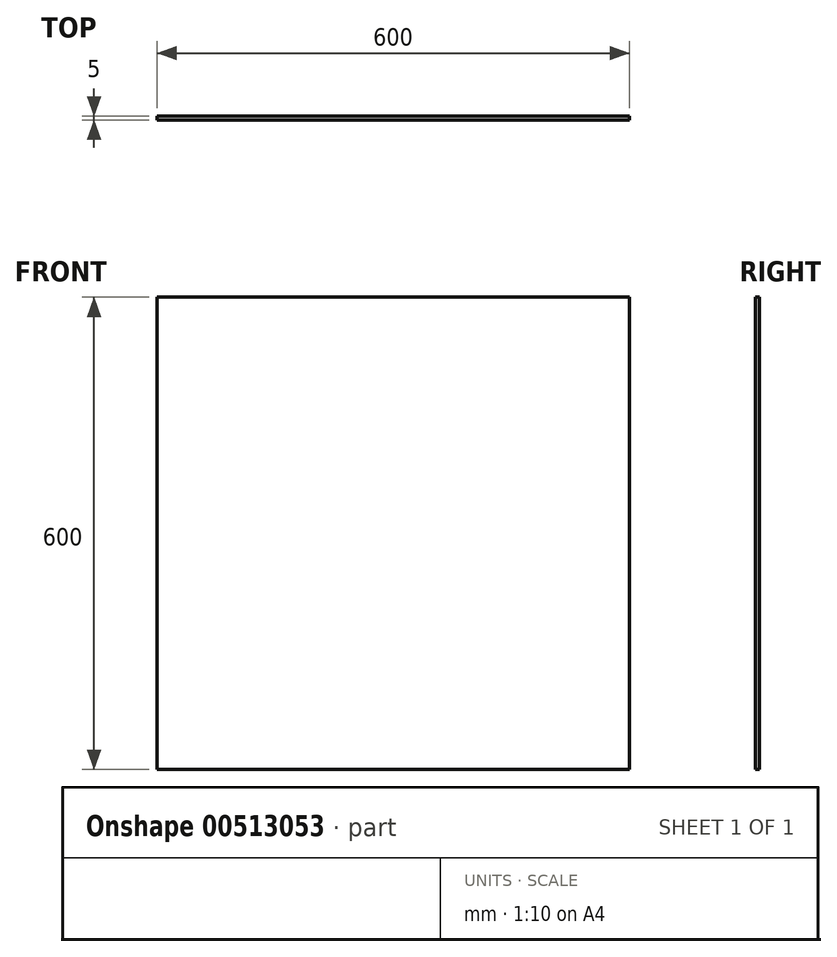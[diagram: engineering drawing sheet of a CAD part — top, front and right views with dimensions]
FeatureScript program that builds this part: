
annotation { "Feature Type Name" : "Feature", "Feature Type Description" : "" }
export const myFeature = defineFeature(function(context is Context, id is Id, definition is map)
    precondition{}
    {
        {
            var Q0;
            Q0=qCreatedBy(makeId("Front.planeOp"),FACE);
            var sketch = newSketch(context, id + "F0", { "sketchPlane" : qUnion([Q0])});
            skLineSegment(sketch, "E0.bottom", {"start": v(300, 300) * mm, "end": v(-300, 300) * mm});
            skLineSegment(sketch, "E0.top", {"start": v(300, -300) * mm, "end": v(-300, -300) * mm});
            skLineSegment(sketch, "E0.left", {"start": v(300, 300) * mm, "end": v(300, -300) * mm});
            skLineSegment(sketch, "E0.right", {"start": v(-300, 300) * mm, "end": v(-300, -300) * mm});
            skPoint(sketch, "E0.middle", {"position": v(0, 0) * mm});
            skSolve(sketch);
        }
        {
            var Q0;
            Q0=makeQuery(id+"F0.imprint","IMPRINT",FACE,{"disambiguationData":[TD([[makeQuery(id+"F0.imprint","IMPRINT",EDGE,{"derivedFrom":sQuery(id+"F0.wireOp",EDGE,"E0.bottom")}),1.0]])]});
            extrude(context, id + "F1", {"entities" : qUnion([Q0]), "oppositeDirection" : true, "depth" : 5 * mm});
        }
    });
